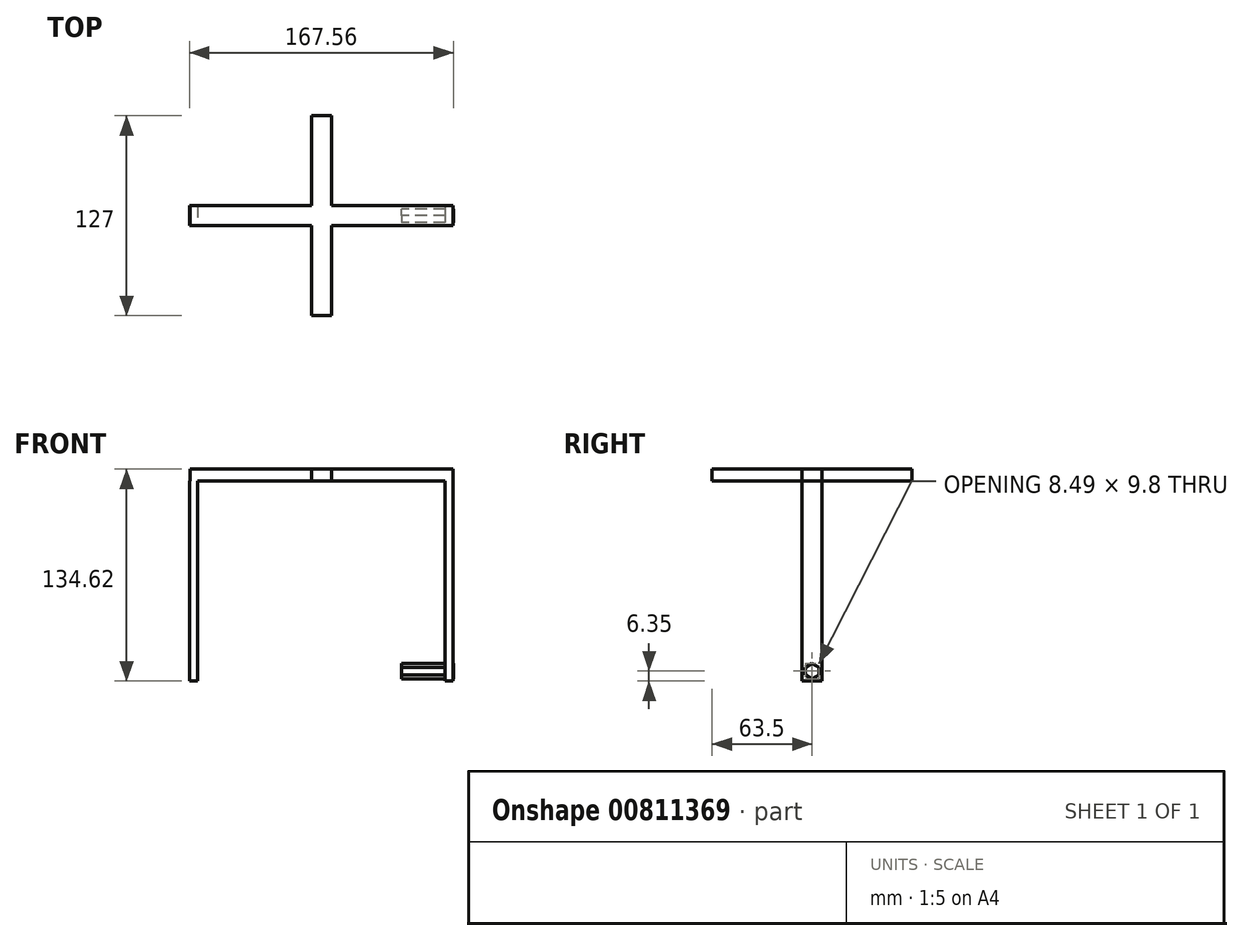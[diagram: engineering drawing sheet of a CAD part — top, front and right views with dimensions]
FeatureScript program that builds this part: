
annotation { "Feature Type Name" : "Feature", "Feature Type Description" : "" }
export const myFeature = defineFeature(function(context is Context, id is Id, definition is map)
    precondition{}
    {
        {
            var Q0;
            Q0=qCreatedBy(makeId("Top.planeOp"),FACE);
            var sketch = newSketch(context, id + "F0", { "sketchPlane" : qUnion([Q0])});
            skLineSegment(sketch, "E0.bottom", {"start": v(83.5, -6.35) * mm, "end": v(-83.5, -6.35) * mm});
            skLineSegment(sketch, "E0.top", {"start": v(83.5, 6.35) * mm, "end": v(-83.5, 6.35) * mm});
            skLineSegment(sketch, "E0.left", {"start": v(83.5, -6.35) * mm, "end": v(83.5, 6.35) * mm});
            skLineSegment(sketch, "E0.right", {"start": v(-83.5, -6.35) * mm, "end": v(-83.5, 6.35) * mm});
            skPoint(sketch, "E0.middle", {"position": v(0, 0) * mm});
            skSolve(sketch);
        }
        {
            var Q0;
            Q0 = qSketchRegion(id + "F0", true);
            extrude(context, id + "F1", {"entities" : qUnion([Q0]), "depth" : 7.62 * mm, "offsetDistance" : 25.4 * mm});
        }
        {
            var Q0;
            Q0=qCreatedBy(makeId("Top.planeOp"),FACE);
            var sketch = newSketch(context, id + "F2", { "sketchPlane" : qUnion([Q0])});
            skLineSegment(sketch, "E1.bottom", {"start": v(-83.74, 6.36) * mm, "end": v(-78.66, 6.36) * mm});
            skLineSegment(sketch, "E1.top", {"start": v(-83.74, -6.34) * mm, "end": v(-78.66, -6.34) * mm});
            skLineSegment(sketch, "E1.left", {"start": v(-83.74, 6.36) * mm, "end": v(-83.74, -6.34) * mm});
            skLineSegment(sketch, "E1.right", {"start": v(-78.66, 6.36) * mm, "end": v(-78.66, -6.34) * mm});
            skSolve(sketch);
        }
        {
            var Q0;
            Q0 = qSketchRegion(id + "F2", true);
            extrude(context, id + "F3", {"entities" : qUnion([Q0]), "operationType" : NewBodyOperationType.ADD, "depth" : -127 * mm, "offsetDistance" : 25.4 * mm});
        }
        {
            var Q0;
            Q0=makeQuery(id+"F1.opExtrude","SWEPT_BODY",BODY,{"disambiguationData":[OSD([sQuery(id+"F0.wireOp",EDGE,"E0.bottom"),sQuery(id+"F0.wireOp",EDGE,"E0.top"),sQuery(id+"F0.wireOp",EDGE,"E0.left"),sQuery(id+"F0.wireOp",EDGE,"E0.right")])]});
            var Q1;
            Q1=qCreatedBy(makeId("Right.planeOp"),FACE);
            mirror(context, id + "F4", {"operationType" : NewBodyOperationType.ADD, "entities" : qUnion([Q0]), "mirrorPlane" : qUnion([Q1])});
        }
        {
            var Q0;
            Q0=qCreatedBy(makeId("Top.planeOp"),FACE);
            var sketch = newSketch(context, id + "F5", { "sketchPlane" : qUnion([Q0])});
            skLineSegment(sketch, "E2.bottom", {"start": v(6.35, -63.5) * mm, "end": v(-6.35, -63.5) * mm});
            skLineSegment(sketch, "E2.top", {"start": v(6.35, 63.5) * mm, "end": v(-6.35, 63.5) * mm});
            skLineSegment(sketch, "E2.left", {"start": v(6.35, -63.5) * mm, "end": v(6.35, 63.5) * mm});
            skLineSegment(sketch, "E2.right", {"start": v(-6.35, -63.5) * mm, "end": v(-6.35, 63.5) * mm});
            skPoint(sketch, "E2.middle", {"position": v(0, 0) * mm});
            skSolve(sketch);
        }
        {
            var Q0;
            Q0 = qSketchRegion(id + "F5", true);
            extrude(context, id + "F6", {"entities" : qUnion([Q0]), "operationType" : NewBodyOperationType.ADD, "depth" : 7.62 * mm, "offsetDistance" : 25.4 * mm});
        }
        {
            var Q0;
            Q0=qCreatedBy(makeId("Right.planeOp"),FACE);
            var sketch = newSketch(context, id + "F7", { "sketchPlane" : qUnion([Q0])});
            skCircle(sketch, "E3.cCircle", {"center": v(0, -120.65) * mm, "radius": 4.9 * mm, "construction": true});
            skLineSegment(sketch, "E3.0", {"start": v(0, -115.75) * mm, "end": v(4.24, -118.2) * mm});
            skLineSegment(sketch, "E3.1", {"start": v(4.24, -118.2) * mm, "end": v(4.24, -123.1) * mm});
            skLineSegment(sketch, "E3.2", {"start": v(4.24, -123.1) * mm, "end": v(0, -125.55) * mm});
            skLineSegment(sketch, "E3.3", {"start": v(0, -125.55) * mm, "end": v(-4.24, -123.1) * mm});
            skLineSegment(sketch, "E3.4", {"start": v(-4.24, -123.1) * mm, "end": v(-4.24, -118.2) * mm});
            skLineSegment(sketch, "E3.5", {"start": v(-4.24, -118.2) * mm, "end": v(0, -115.75) * mm});
            skSolve(sketch);
        }
        {
            var Q0;
            Q0 = qSketchRegion(id + "F7", true);
            extrude(context, id + "F8", {"entities" : qUnion([Q0]), "operationType" : NewBodyOperationType.ADD, "depth" : 83.82 * mm, "offsetDistance" : 25.4 * mm, "hasSecondDirection" : true, "secondDirectionOppositeDirection" : true, "secondDirectionDepth" : -50.8 * mm});
        }
    });
